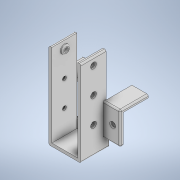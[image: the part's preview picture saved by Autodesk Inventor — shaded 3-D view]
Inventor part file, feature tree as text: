
AUTODESK INVENTOR PART (.ipt)
format: ipt  version: 2020 (Build 240168000, 168)  size: 293,888 bytes
history: native  units: in
note: dims shown in document units (in); Inventor stores cm internally (conversion verified against a paired STEP export)
features: extrude x11, sketch x11, fillet x3, mirror x2, pattern_linear x1
ambient origin geometry x8: Origin, YZ Plane, XZ Plane, XY Plane, X Axis, Y Axis, Z Axis, Center Point
bodies: Solid1 (feature_tree)
feature tree (28):
  extrude  "Extrusion1"  Depth=1.0in
  extrude  "Extrusion2"  Depth=0.1181in
  extrude  "Extrusion3"  Depth=3.2972in TaperAngle=0.0deg
  extrude  "Extrusion4"  Depth=0.1181in TaperAngle=0.0deg
  extrude  "Extrusion5"  Depth=0.0591in TaperAngle=0.0deg
  fillet  "Fillet1"  Radius=0.3346in
  pattern_linear  "Rectangular Pattern1"  Count1=3 Spacing1=-1.0236in
  mirror  "Mirror2"
  extrude  "Extrusion6"  Depth=1.2756in
  extrude  "Extrusion7"  Depth=0.6811in
  extrude  "Extrusion8"  Depth=0.2362in
  extrude  "Extrusion9"  Depth=0.0591in
  fillet  "Fillet2"  Radius=0.0787in
  extrude  "Extrusion11"  Depth=0.0591in
  extrude  "Extrusion14"  Depth=0.1181in TaperAngle=0.0deg
  mirror  "Mirror4"
  fillet  "Fillet5"  Radius=0.6496in
  sketch  "Sketch1"  dims[d0=1.2756in d1=1.0in]
  sketch  "Sketch2"  dims[d2=0.1181in d3=0.0in d4=0.1181in]
  sketch  "Sketch3"  dims[d5=0.1181in d6=3.2972in d7=0.0in]
  sketch  "Sketch4"  dims[d8=0.1575in d9=0.1181in d10=0.0in]
  sketch  "Sketch5"  dims[d11=0.2362in d12=0.0591in d13=0.0in d14=0.3346in]
  sketch  "Sketch6"  dims[d15=0.0787in d16=0.0in]
  sketch  "Sketch7"  dims[d17=0.0472in d18=1.1811in d20=-1.0236in]
  sketch  "Sketch8"  dims[d21=0.1181in d22=1.2756in]
  sketch  "Sketch9"  dims[d23=0.6811in d24=0.0in d25=0.1575in]
  sketch  "Sketch11"  dims[d26=0.1181in d27=0.0in d28=0.2362in]
  sketch  "Sketch14"  dims[d29=0.0591in d30=0.0in d31=0.3346in d32=0.0787in d33=0.0in d34=0.0591in d38=0.1181in d39=0.0in d48=0.6496in d49=0.1181in d50=1.0in d51=0.0in d53=0.0591in]
